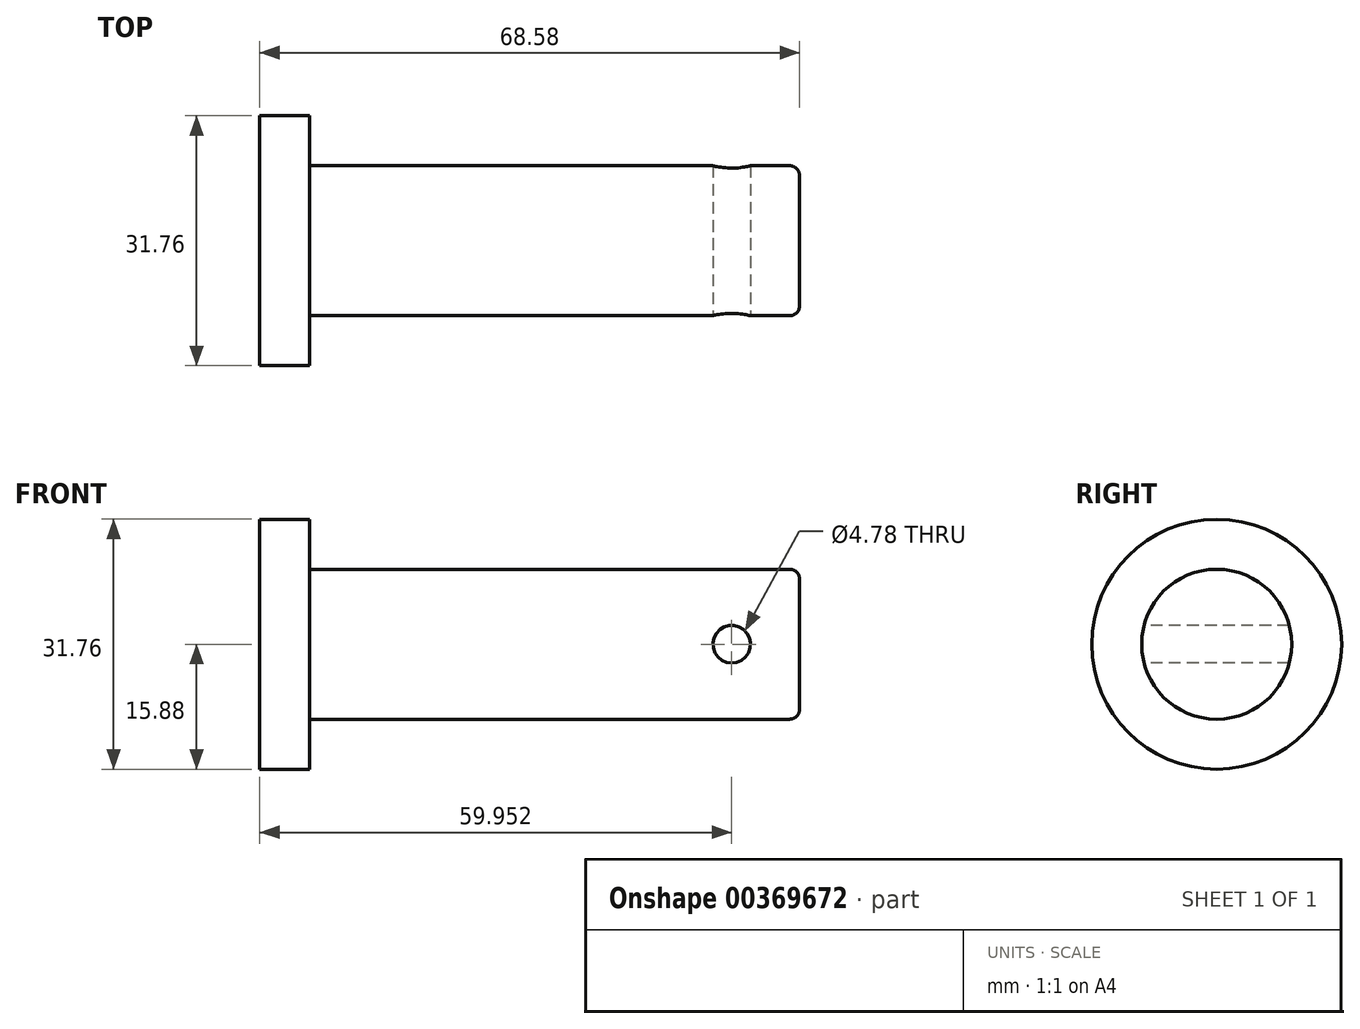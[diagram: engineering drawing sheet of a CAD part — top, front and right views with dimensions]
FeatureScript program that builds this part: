
annotation { "Feature Type Name" : "Feature", "Feature Type Description" : "" }
export const myFeature = defineFeature(function(context is Context, id is Id, definition is map)
    precondition{}
    {
        {
            var Q0;
            Q0=qCreatedBy(makeId("Right.planeOp"),FACE);
            var sketch = newSketch(context, id + "F0", { "sketchPlane" : qUnion([Q0])});
            skCircle(sketch, "E0", {"center": v(0, 0) * mm, "radius": 15.88 * mm});
            skSolve(sketch);
        }
        {
            var Q0;
            Q0 = qSketchRegion(id + "F0", true);
            extrude(context, id + "F1", {"entities" : qUnion([Q0]), "depth" : 6.35 * mm});
        }
        {
            var Q0;
            Q0=makeQuery(id+"F1.opExtrude","CAP_FACE",FACE,{"disambiguationData":[OSD([sQuery(id+"F0.wireOp",EDGE,"E0")])],"isStart":false});
            var sketch = newSketch(context, id + "F2", { "sketchPlane" : qUnion([Q0])});
            skCircle(sketch, "E1", {"center": v(0, 0) * mm, "radius": 9.53 * mm});
            skSolve(sketch);
        }
        {
            var Q0;
            Q0 = qSketchRegion(id + "F2", true);
            extrude(context, id + "F3", {"entities" : qUnion([Q0]), "operationType" : NewBodyOperationType.ADD, "depth" : 62.23 * mm});
        }
        {
            var Q0;
            Q0=makeQuery(id+"F3.opExtrude","CAP_EDGE",EDGE,{"disambiguationData":[OSD([sQuery(id+"F2.wireOp",EDGE,"E1")])],"isStart":false});
            fillet(context, id + "F4", {"entities" : qUnion([Q0]), "radius" : 1.27 * mm, "tangentPropagation" : true, "allowEdgeOverflow" : false});
        }
        {
            var Q0;
            Q0=qCreatedBy(makeId("Front.planeOp"),FACE);
            var sketch = newSketch(context, id + "F5", { "sketchPlane" : qUnion([Q0])});
            skLineSegment(sketch, "E2", {"start": v(66.3, 0) * mm, "end": v(59.95, 0) * mm, "construction": true});
            skCircle(sketch, "E3", {"center": v(59.95, 0) * mm, "radius": 2.39 * mm});
            skSolve(sketch);
        }
        {
            var Q0;
            Q0 = qSketchRegion(id + "F5", true);
            extrude(context, id + "F6", {"entities" : qUnion([Q0]), "operationType" : NewBodyOperationType.REMOVE, "endBound" : BoundingType.SYMMETRIC, "oppositeDirection" : true, "depth" : 25.4 * mm});
        }
    });
